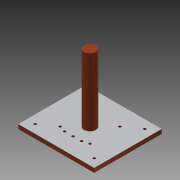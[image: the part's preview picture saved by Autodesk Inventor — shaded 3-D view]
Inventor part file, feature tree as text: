
AUTODESK INVENTOR PART (.ipt)
format: ipt  version: 2013 (Build 170138000, 138)  size: 140,288 bytes
history: native  units: mm
features: sketch x7, extrude x4, hole x2, other x1
ambient origin geometry x8: Origin, YZ Plane, XZ Plane, XY Plane, X Axis, Y Axis, Z Axis, Center Point
feature tree (14):
  other  "ソリッド1"
  extrude  "押し出し1"  Depth=5.0mm TaperAngle=0.0deg
  extrude  "押し出し2"  Depth=5.0mm TaperAngle=0.0deg
  extrude  "押し出し3"  Depth=5.0mm TaperAngle=0.0deg
  hole  "穴1"  [1 undecoded]
  sketch  "スケッチ5"
  sketch  "スケッチ6"
  extrude  "押し出し4"  Depth=10.0mm
  hole  "穴2"  [1 undecoded]
  sketch  "スケッチ1"
  sketch  "スケッチ2"
  sketch  "スケッチ3"
  sketch  "スケッチ4"
  sketch  "スケッチ7"
note: 2 required parameter values undecoded (feature->parameter linkage not recoverable at this tier; creation-order binding heuristic only, values carry confidence <= 0.55)
